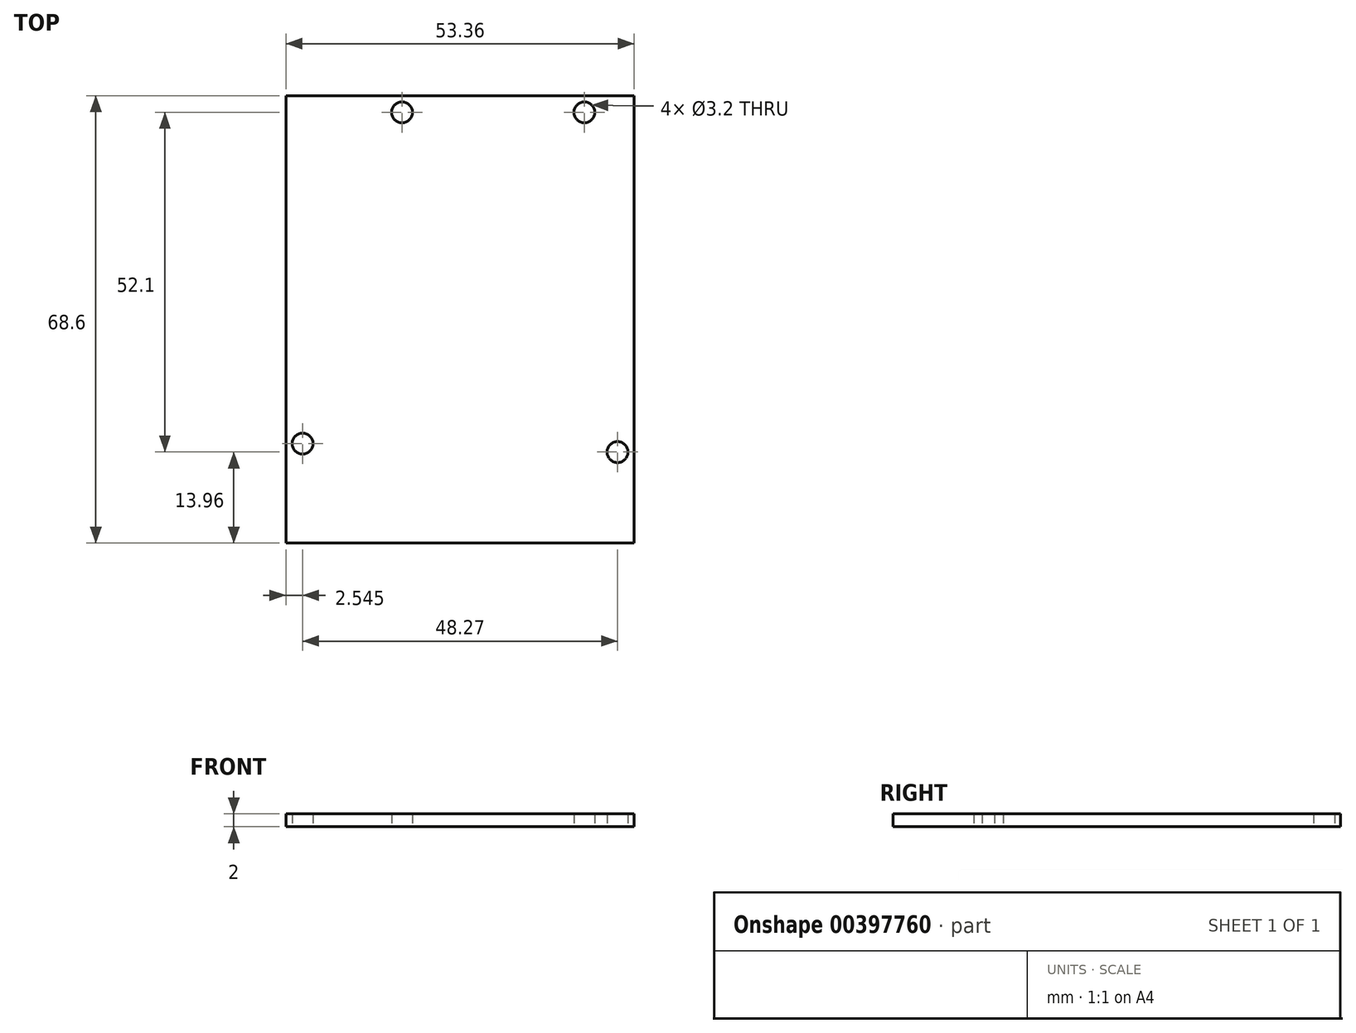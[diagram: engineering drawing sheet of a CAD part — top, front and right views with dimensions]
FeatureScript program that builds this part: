
annotation { "Feature Type Name" : "Feature", "Feature Type Description" : "" }
export const myFeature = defineFeature(function(context is Context, id is Id, definition is map)
    precondition{}
    {
        {
            var Q0;
            Q0=qCreatedBy(makeId("Top.planeOp"),FACE);
            var sketch = newSketch(context, id + "F0", { "sketchPlane" : qUnion([Q0])});
            skLineSegment(sketch, "E0.bottom", {"start": v(26.67, -34.3) * mm, "end": v(-26.68, -34.3) * mm});
            skLineSegment(sketch, "E0.top", {"start": v(26.67, 34.3) * mm, "end": v(-26.68, 34.3) * mm});
            skLineSegment(sketch, "E0.left", {"start": v(26.67, -34.3) * mm, "end": v(26.67, 34.3) * mm});
            skLineSegment(sketch, "E0.right", {"start": v(-26.68, -34.3) * mm, "end": v(-26.68, 34.3) * mm});
            skPoint(sketch, "E0.middle", {"position": v(0, 0) * mm});
            skCircle(sketch, "E1", {"center": v(-8.9, 31.76) * mm, "radius": 1.6 * mm});
            skCircle(sketch, "E2", {"center": v(19.05, 31.76) * mm, "radius": 1.6 * mm});
            skCircle(sketch, "E3", {"center": v(-24.14, -19.04) * mm, "radius": 1.6 * mm});
            skCircle(sketch, "E4", {"center": v(24.13, -20.34) * mm, "radius": 1.6 * mm});
            skSolve(sketch);
        }
        {
            var Q0;
            Q0 = qSketchRegion(id + "F0", true);
            extrude(context, id + "F1", {"entities" : qUnion([Q0]), "depth" : 2 * mm});
        }
    });
